# Revit family: Storage-Teknion-AFML-Audience_Laminate_Hospitality_Cart-R2018
name_source: partatom
category: Furniture
revit_build: Autodesk Revit 2018 (Build: 20170223_1515(x64)
units: mm (PartAtom-declared; Revit-internal decimal feet)

## family parameters
Always vertical = Yes
Cut with Voids When Loaded = No
OmniClass Number = 23.40.20.00
OmniClass Title = General Furniture and Specialties
Room Calculation Point = No
Shared = Yes
Work Plane-Based = No

## types (4) — shared parameters
Assembly Code = E2020200
Manufacturer = Teknion
Manufacturer Fax = 416.661.4586
Part Number = AFML
Product Documentation Link = https://www.teknion.com
Product Line = Tables & Collaborative Spaces
Product Page URL = http://www.teknion.com
Series = Tables & Collaborative Spaces
Sustainability Data = https://www.teknion.com
URL = www.teknion.com
Unit Weight URL = http://www.teknion.com
Warranty = http://www.teknion.com

## per-type parameters (varying)
| type | Cutout Offset | Description | Glass | Glass Doors | Glass Doors and Drawers | Model | One Handle | Solid Doors | Solid Doors and Drawers | Two Door | Two Handle | Two Handle High | Two Handle Low |
| Door Configuration, Solid Door, 32" Width, 36" Height | 33.599 " | Audience Laminate Hospitality Cart, Doors Configuration, Solid Door, 32" Width, 36" Height | No | No | No | AFMLAS3236 | No | Yes | No | Yes | Yes | Yes | No |
| Door & Drawers Configuration, Solid Door, 32" Width, 36" Height | 29.357 " | Audience Laminate Hospitality Cart, Doors & Drawers Configuration, Solid Door, 32" Width, 36" Height | No | No | No | AFMLBS3236 | Yes | No | Yes | No | Yes | No | Yes |
| Door Configuration, Glass Door, 32" Width, 36" Height | 33.599 " | Audience Laminate Hospitality Cart, Doors Configuration, Glass Door, 32" Width, 36" Height | Yes | Yes | No | AFMLAG3236 | No | No | No | Yes | No | No | No |
| Door & Drawers Configuration, Glass Door, 32" Width, 36" Height | 29.357 " | Audience Laminate Hospitality Cart, Doors & Drawers Configuration, Glass Door, 32" Width, 36" Height | Yes | No | Yes | AFMLBG3236 | Yes | No | No | No | No | No | No |

## geometry (parser evidence)
native form markers: Sweep x2
no freeform markers — native parametric forms only
